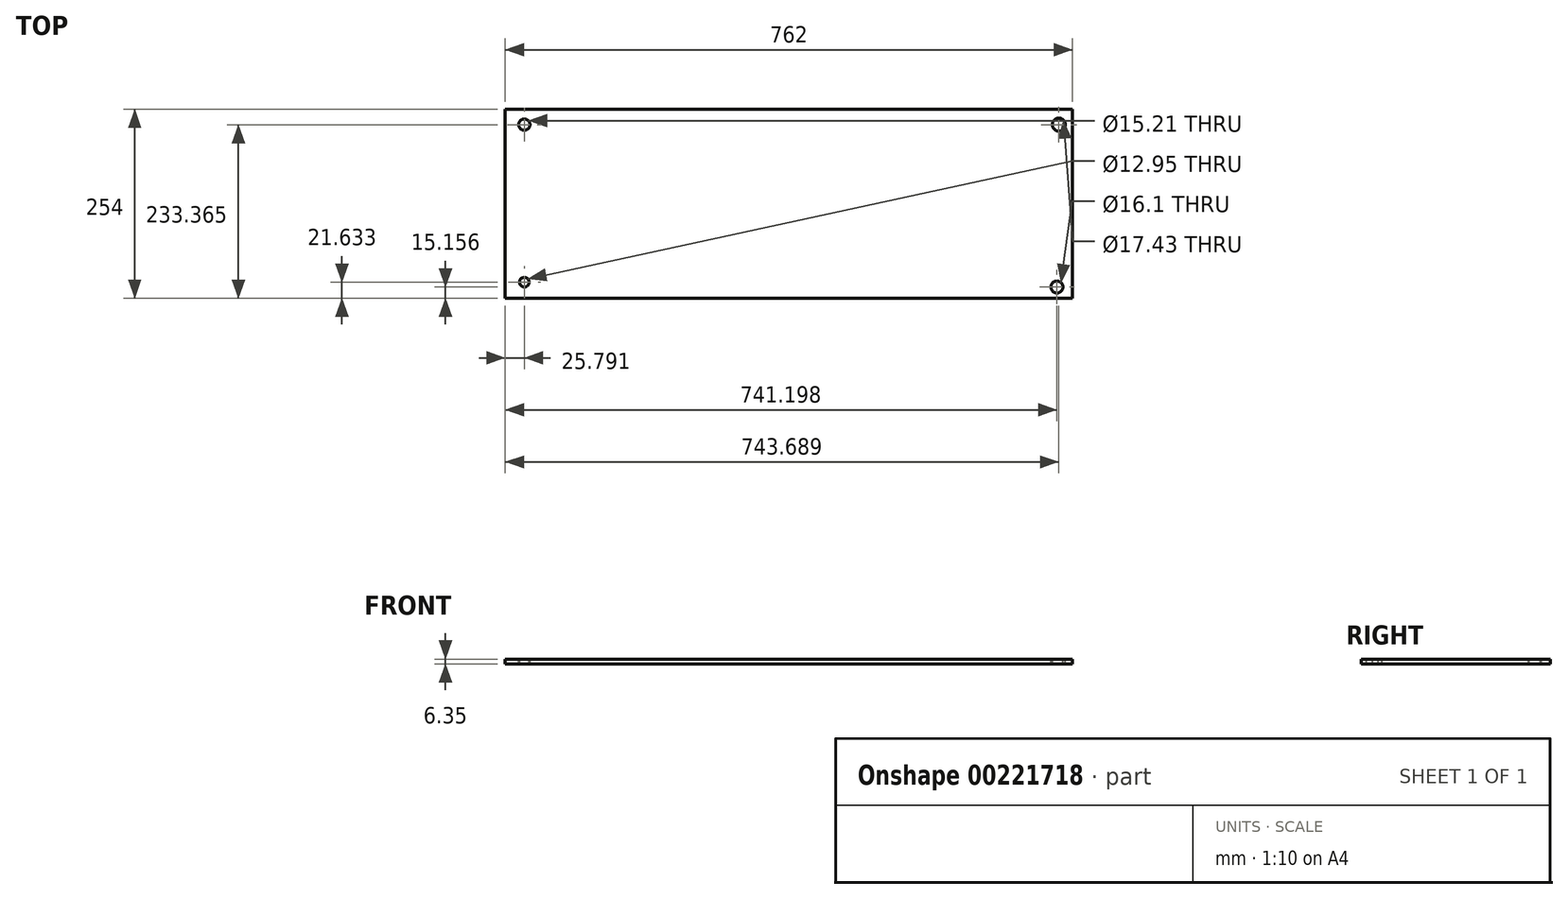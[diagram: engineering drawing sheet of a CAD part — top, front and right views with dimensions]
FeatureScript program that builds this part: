
annotation { "Feature Type Name" : "Feature", "Feature Type Description" : "" }
export const myFeature = defineFeature(function(context is Context, id is Id, definition is map)
    precondition{}
    {
        {
            var Q0;
            Q0=qCreatedBy(makeId("Top.planeOp"),FACE);
            var sketch = newSketch(context, id + "F0", { "sketchPlane" : qUnion([Q0])});
            skLineSegment(sketch, "E0.bottom", {"start": v(-431.09, -121.95) * mm, "end": v(330.91, -121.95) * mm});
            skLineSegment(sketch, "E0.top", {"start": v(-431.09, 132.05) * mm, "end": v(330.91, 132.05) * mm});
            skLineSegment(sketch, "E0.left", {"start": v(-431.09, -121.95) * mm, "end": v(-431.09, 132.05) * mm});
            skLineSegment(sketch, "E0.right", {"start": v(330.91, -121.95) * mm, "end": v(330.91, 132.05) * mm});
            skSolve(sketch);
        }
        {
            var Q0;
            Q0=makeQuery(id+"F0.imprint","IMPRINT",FACE,{"disambiguationData":[TD([[makeQuery(id+"F0.imprint","IMPRINT",EDGE,{"derivedFrom":sQuery(id+"F0.wireOp",EDGE,"E0.bottom")}),1.0]])]});
            extrude(context, id + "F1", {"entities" : qUnion([Q0]), "oppositeDirection" : true, "depth" : 6.35 * mm});
        }
        {
            var Q0;
            Q0=makeQuery(id+"F1.opExtrude","CAP_FACE",FACE,{"disambiguationData":[OSD([sQuery(id+"F0.wireOp",EDGE,"E0.bottom"),sQuery(id+"F0.wireOp",EDGE,"E0.top"),sQuery(id+"F0.wireOp",EDGE,"E0.left"),sQuery(id+"F0.wireOp",EDGE,"E0.right")])],"isStart":true});
            var sketch = newSketch(context, id + "F2", { "sketchPlane" : qUnion([Q0])});
            skCircle(sketch, "E1", {"center": v(-405.3, 111.42) * mm, "radius": 7.6 * mm});
            skCircle(sketch, "E2", {"center": v(-405.3, -100.32) * mm, "radius": 6.48 * mm});
            skCircle(sketch, "E3", {"center": v(310.1, -106.8) * mm, "radius": 8.05 * mm});
            skCircle(sketch, "E4", {"center": v(312.6, 111.42) * mm, "radius": 8.71 * mm});
            skSolve(sketch);
        }
        {
            var Q0;
            Q0=makeQuery(id+"F2.imprint","IMPRINT",FACE,{"disambiguationData":[TD([[makeQuery(id+"F2.imprint","IMPRINT",EDGE,{"derivedFrom":sQuery(id+"F2.wireOp",EDGE,"E1")}),1.0]])]});
            var Q1;
            Q1=makeQuery(id+"F2.imprint","IMPRINT",FACE,{"disambiguationData":[TD([[makeQuery(id+"F2.imprint","IMPRINT",EDGE,{"derivedFrom":sQuery(id+"F2.wireOp",EDGE,"E2")}),1.0]])]});
            var Q2;
            Q2=makeQuery(id+"F2.imprint","IMPRINT",FACE,{"disambiguationData":[TD([[makeQuery(id+"F2.imprint","IMPRINT",EDGE,{"derivedFrom":sQuery(id+"F2.wireOp",EDGE,"E3")}),1.0]])]});
            var Q3;
            Q3=makeQuery(id+"F2.imprint","IMPRINT",FACE,{"disambiguationData":[TD([[makeQuery(id+"F2.imprint","IMPRINT",EDGE,{"derivedFrom":sQuery(id+"F2.wireOp",EDGE,"E4")}),1.0]])]});
            extrude(context, id + "F3", {"entities" : qUnion([Q0, Q1, Q2, Q3]), "operationType" : NewBodyOperationType.REMOVE, "oppositeDirection" : true, "depth" : 25.4 * mm});
        }
    });
